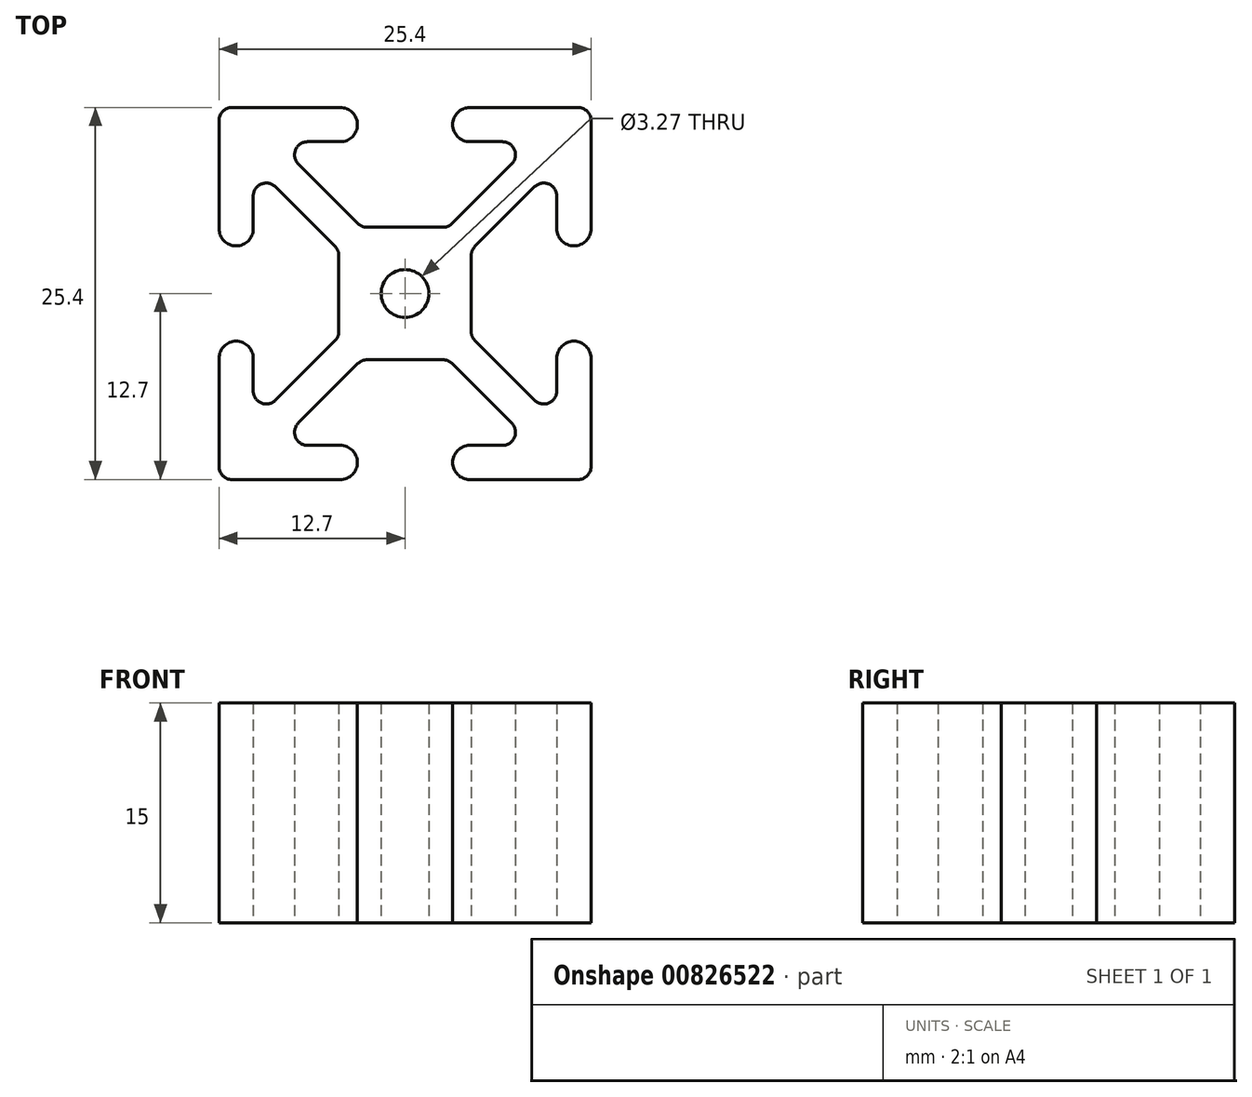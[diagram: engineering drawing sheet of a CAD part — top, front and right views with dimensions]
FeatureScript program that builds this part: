
annotation { "Feature Type Name" : "Feature", "Feature Type Description" : "" }
export const myFeature = defineFeature(function(context is Context, id is Id, definition is map)
    precondition{}
    {
        {
            assignVariable(context, id + "F0", {"name" : "SPINE_length", "anyValue" : 15});
        }
        {
            var Q0;
            Q0=qCreatedBy(makeId("Top.planeOp"),FACE);
            var sketch = newSketch(context, id + "F1", { "sketchPlane" : qUnion([Q0])});
            skCircle(sketch, "E0", {"center": v(0, 0) * mm, "radius": 1.63 * mm});
            skLineSegment(sketch, "E1.bottom", {"start": v(2.6, -4.52) * mm, "end": v(-2.6, -4.52) * mm});
            skLineSegment(sketch, "E1.top", {"start": v(2.6, 4.52) * mm, "end": v(-2.6, 4.52) * mm});
            skLineSegment(sketch, "E1.left", {"start": v(4.52, -2.6) * mm, "end": v(4.52, 2.6) * mm});
            skLineSegment(sketch, "E1.right", {"start": v(-4.52, -2.6) * mm, "end": v(-4.52, 2.6) * mm});
            skLineSegment(sketch, "E2", {"start": v(-3.22, -4.78) * mm, "end": v(-7.28, -8.85) * mm});
            skLineSegment(sketch, "E3", {"start": v(-4.78, -3.22) * mm, "end": v(-8.85, -7.28) * mm});
            skLineSegment(sketch, "E4", {"start": v(-4.52, -4.52) * mm, "end": v(4.52, 4.52) * mm, "construction": true});
            skLineSegment(sketch, "E5", {"start": v(-4.52, 4.52) * mm, "end": v(4.52, -4.52) * mm, "construction": true});
            skLineSegment(sketch, "E6", {"start": v(-3.22, 4.78) * mm, "end": v(-7.28, 8.85) * mm});
            skLineSegment(sketch, "E7", {"start": v(-4.78, 3.22) * mm, "end": v(-8.85, 7.28) * mm});
            skLineSegment(sketch, "E8", {"start": v(3.22, 4.78) * mm, "end": v(7.28, 8.85) * mm});
            skLineSegment(sketch, "E9", {"start": v(4.78, 3.22) * mm, "end": v(8.85, 7.28) * mm});
            skLineSegment(sketch, "E10", {"start": v(4.78, -3.22) * mm, "end": v(8.85, -7.28) * mm});
            skLineSegment(sketch, "E11", {"start": v(3.22, -4.78) * mm, "end": v(7.28, -8.85) * mm});
            skLineSegment(sketch, "E12", {"start": v(-6.65, -10.36) * mm, "end": v(-4.42, -10.36) * mm});
            skLineSegment(sketch, "E13", {"start": v(-10.36, -6.65) * mm, "end": v(-10.36, -4.42) * mm});
            skLineSegment(sketch, "E14", {"start": v(-10.36, 6.65) * mm, "end": v(-10.36, 4.42) * mm});
            skLineSegment(sketch, "E15", {"start": v(-6.65, 10.36) * mm, "end": v(-4.42, 10.36) * mm});
            skLineSegment(sketch, "E16", {"start": v(6.65, 10.36) * mm, "end": v(4.42, 10.36) * mm});
            skLineSegment(sketch, "E17", {"start": v(10.36, 6.65) * mm, "end": v(10.36, 4.42) * mm});
            skLineSegment(sketch, "E18", {"start": v(10.36, -6.65) * mm, "end": v(10.36, -4.42) * mm});
            skLineSegment(sketch, "E19", {"start": v(6.65, -10.36) * mm, "end": v(4.42, -10.36) * mm});
            skLineSegment(sketch, "E20", {"start": v(-4.42, 12.7) * mm, "end": v(-11.81, 12.7) * mm});
            skLineSegment(sketch, "E21", {"start": v(-12.7, 11.81) * mm, "end": v(-12.7, 4.42) * mm});
            skLineSegment(sketch, "E22", {"start": v(-12.7, -11.81) * mm, "end": v(-12.7, -4.42) * mm});
            skLineSegment(sketch, "E23", {"start": v(-11.81, -12.7) * mm, "end": v(-4.42, -12.7) * mm});
            skLineSegment(sketch, "E24", {"start": v(11.81, -12.7) * mm, "end": v(4.42, -12.7) * mm});
            skLineSegment(sketch, "E25", {"start": v(12.7, -11.81) * mm, "end": v(12.7, -4.42) * mm});
            skLineSegment(sketch, "E26", {"start": v(12.7, 11.81) * mm, "end": v(12.7, 4.42) * mm});
            skLineSegment(sketch, "E27", {"start": v(11.81, 12.7) * mm, "end": v(4.42, 12.7) * mm});
            skLineSegment(sketch, "E28", {"start": v(-11.48, 3.25) * mm, "end": v(-11.48, 3.25) * mm});
            skLineSegment(sketch, "E29", {"start": v(-11.59, -3.25) * mm, "end": v(-11.59, -3.25) * mm});
            skLineSegment(sketch, "E30", {"start": v(-3.25, -11.53) * mm, "end": v(-3.25, -11.53) * mm});
            skLineSegment(sketch, "E31", {"start": v(3.25, -11.53) * mm, "end": v(3.25, -11.53) * mm});
            skLineSegment(sketch, "E32", {"start": v(11.53, -3.25) * mm, "end": v(11.53, -3.25) * mm});
            skLineSegment(sketch, "E33", {"start": v(11.53, 3.25) * mm, "end": v(11.53, 3.25) * mm});
            skLineSegment(sketch, "E34", {"start": v(3.25, 11.53) * mm, "end": v(3.25, 11.53) * mm});
            skLineSegment(sketch, "E35", {"start": v(-3.25, 11.53) * mm, "end": v(-3.25, 11.53) * mm});
            skPoint(sketch, "E36.visualSharp", {"position": v(-8.8, 10.36) * mm});
            skArc(sketch, "E36.filletArc", {"start": v(-6.65, 10.36) * mm, "mid": v(-7.48, 9.81) * mm, "end": v(-7.28, 8.85) * mm});
            skPoint(sketch, "E37.visualSharp", {"position": v(8.8, 10.36) * mm});
            skArc(sketch, "E37.filletArc", {"start": v(7.28, 8.85) * mm, "mid": v(7.48, 9.81) * mm, "end": v(6.65, 10.36) * mm});
            skPoint(sketch, "E38.visualSharp", {"position": v(10.36, 8.8) * mm});
            skArc(sketch, "E38.filletArc", {"start": v(10.36, 6.65) * mm, "mid": v(9.81, 7.48) * mm, "end": v(8.85, 7.28) * mm});
            skPoint(sketch, "E39.visualSharp", {"position": v(10.36, -8.8) * mm});
            skArc(sketch, "E39.filletArc", {"start": v(8.85, -7.28) * mm, "mid": v(9.81, -7.48) * mm, "end": v(10.36, -6.65) * mm});
            skPoint(sketch, "E40.visualSharp", {"position": v(8.8, -10.36) * mm});
            skArc(sketch, "E40.filletArc", {"start": v(6.65, -10.36) * mm, "mid": v(7.48, -9.81) * mm, "end": v(7.28, -8.85) * mm});
            skPoint(sketch, "E41.visualSharp", {"position": v(-10.36, -8.8) * mm});
            skArc(sketch, "E41.filletArc", {"start": v(-10.36, -6.65) * mm, "mid": v(-9.81, -7.48) * mm, "end": v(-8.85, -7.28) * mm});
            skPoint(sketch, "E42.visualSharp", {"position": v(-8.8, -10.36) * mm});
            skArc(sketch, "E42.filletArc", {"start": v(-7.28, -8.85) * mm, "mid": v(-7.48, -9.81) * mm, "end": v(-6.65, -10.36) * mm});
            skPoint(sketch, "E43.visualSharp", {"position": v(-10.36, 8.8) * mm});
            skArc(sketch, "E43.filletArc", {"start": v(-8.85, 7.28) * mm, "mid": v(-9.81, 7.48) * mm, "end": v(-10.36, 6.65) * mm});
            skPoint(sketch, "E44.visualSharp", {"position": v(-12.7, 12.7) * mm});
            skArc(sketch, "E44.filletArc", {"start": v(-11.81, 12.7) * mm, "mid": v(-12.44, 12.44) * mm, "end": v(-12.7, 11.81) * mm});
            skPoint(sketch, "E45.visualSharp", {"position": v(12.7, 12.7) * mm});
            skArc(sketch, "E45.filletArc", {"start": v(12.7, 11.81) * mm, "mid": v(12.44, 12.44) * mm, "end": v(11.81, 12.7) * mm});
            skPoint(sketch, "E46.visualSharp", {"position": v(12.7, -12.7) * mm});
            skArc(sketch, "E46.filletArc", {"start": v(11.81, -12.7) * mm, "mid": v(12.44, -12.44) * mm, "end": v(12.7, -11.81) * mm});
            skPoint(sketch, "E47.visualSharp", {"position": v(-12.7, -12.7) * mm});
            skArc(sketch, "E47.filletArc", {"start": v(-12.7, -11.81) * mm, "mid": v(-12.44, -12.44) * mm, "end": v(-11.81, -12.7) * mm});
            skPoint(sketch, "E48.newPointB", {"position": v(-6.36, 4.52) * mm});
            skArc(sketch, "E48.filletArc", {"start": v(-3.22, 4.78) * mm, "mid": v(-2.93, 4.59) * mm, "end": v(-2.6, 4.52) * mm});
            skPoint(sketch, "E49.newPointB", {"position": v(2.6, 4.52) * mm});
            skArc(sketch, "E49.filletArc", {"start": v(2.6, 4.52) * mm, "mid": v(2.93, 4.59) * mm, "end": v(3.22, 4.78) * mm});
            skArc(sketch, "E50.filletArc", {"start": v(4.78, 3.22) * mm, "mid": v(4.59, 2.93) * mm, "end": v(4.52, 2.6) * mm});
            skArc(sketch, "E51.filletArc", {"start": v(-4.78, -3.22) * mm, "mid": v(-4.59, -2.93) * mm, "end": v(-4.52, -2.6) * mm});
            skPoint(sketch, "E52.newPointA", {"position": v(-2.6, -4.52) * mm});
            skArc(sketch, "E52.filletArc", {"start": v(-2.6, -4.52) * mm, "mid": v(-2.93, -4.59) * mm, "end": v(-3.22, -4.78) * mm});
            skArc(sketch, "E53.filletArc", {"start": v(4.52, -2.6) * mm, "mid": v(4.59, -2.93) * mm, "end": v(4.78, -3.22) * mm});
            skPoint(sketch, "E54.newPointA", {"position": v(6.36, -4.52) * mm});
            skArc(sketch, "E54.filletArc", {"start": v(3.22, -4.78) * mm, "mid": v(2.93, -4.59) * mm, "end": v(2.6, -4.52) * mm});
            skArc(sketch, "E55.filletArc", {"start": v(-4.52, 2.6) * mm, "mid": v(-4.59, 2.93) * mm, "end": v(-4.78, 3.22) * mm});
            skPoint(sketch, "E56.visualSharp", {"position": v(-12.7, 3.2) * mm});
            skArc(sketch, "E56.filletArc", {"start": v(-12.7, 4.42) * mm, "mid": v(-12.34, 3.58) * mm, "end": v(-11.48, 3.25) * mm});
            skPoint(sketch, "E57.visualSharp", {"position": v(-10.36, 3.3) * mm});
            skArc(sketch, "E57.filletArc", {"start": v(-11.48, 3.25) * mm, "mid": v(-10.69, 3.61) * mm, "end": v(-10.36, 4.42) * mm});
            skPoint(sketch, "E58.visualSharp", {"position": v(-3.25, 12.7) * mm});
            skArc(sketch, "E58.filletArc", {"start": v(-3.25, 11.53) * mm, "mid": v(-3.6, 12.36) * mm, "end": v(-4.42, 12.7) * mm});
            skPoint(sketch, "E59.visualSharp", {"position": v(-3.25, 10.36) * mm});
            skArc(sketch, "E59.filletArc", {"start": v(-4.42, 10.36) * mm, "mid": v(-3.6, 10.7) * mm, "end": v(-3.25, 11.53) * mm});
            skPoint(sketch, "E60.visualSharp", {"position": v(3.25, 10.36) * mm});
            skArc(sketch, "E60.filletArc", {"start": v(3.25, 11.53) * mm, "mid": v(3.6, 10.7) * mm, "end": v(4.42, 10.36) * mm});
            skPoint(sketch, "E61.visualSharp", {"position": v(3.25, 12.7) * mm});
            skArc(sketch, "E61.filletArc", {"start": v(4.42, 12.7) * mm, "mid": v(3.6, 12.36) * mm, "end": v(3.25, 11.53) * mm});
            skPoint(sketch, "E62.visualSharp", {"position": v(10.36, 3.25) * mm});
            skArc(sketch, "E62.filletArc", {"start": v(10.36, 4.42) * mm, "mid": v(10.7, 3.6) * mm, "end": v(11.53, 3.25) * mm});
            skPoint(sketch, "E63.visualSharp", {"position": v(12.7, 3.25) * mm});
            skArc(sketch, "E63.filletArc", {"start": v(11.53, 3.25) * mm, "mid": v(12.36, 3.6) * mm, "end": v(12.7, 4.42) * mm});
            skPoint(sketch, "E64.visualSharp", {"position": v(12.7, -3.25) * mm});
            skArc(sketch, "E64.filletArc", {"start": v(12.7, -4.42) * mm, "mid": v(12.36, -3.6) * mm, "end": v(11.53, -3.25) * mm});
            skPoint(sketch, "E65.visualSharp", {"position": v(10.36, -3.25) * mm});
            skArc(sketch, "E65.filletArc", {"start": v(11.53, -3.25) * mm, "mid": v(10.7, -3.6) * mm, "end": v(10.36, -4.42) * mm});
            skPoint(sketch, "E66.visualSharp", {"position": v(3.25, -10.36) * mm});
            skArc(sketch, "E66.filletArc", {"start": v(4.42, -10.36) * mm, "mid": v(3.6, -10.7) * mm, "end": v(3.25, -11.53) * mm});
            skPoint(sketch, "E67.visualSharp", {"position": v(3.25, -12.7) * mm});
            skArc(sketch, "E67.filletArc", {"start": v(3.25, -11.53) * mm, "mid": v(3.6, -12.36) * mm, "end": v(4.42, -12.7) * mm});
            skPoint(sketch, "E68.visualSharp", {"position": v(-3.25, -12.7) * mm});
            skArc(sketch, "E68.filletArc", {"start": v(-4.42, -12.7) * mm, "mid": v(-3.6, -12.36) * mm, "end": v(-3.25, -11.53) * mm});
            skPoint(sketch, "E69.visualSharp", {"position": v(-3.25, -10.36) * mm});
            skArc(sketch, "E69.filletArc", {"start": v(-3.25, -11.53) * mm, "mid": v(-3.6, -10.7) * mm, "end": v(-4.42, -10.36) * mm});
            skPoint(sketch, "E70.visualSharp", {"position": v(-10.36, -3.2) * mm});
            skArc(sketch, "E70.filletArc", {"start": v(-10.36, -4.42) * mm, "mid": v(-10.73, -3.58) * mm, "end": v(-11.59, -3.25) * mm});
            skPoint(sketch, "E71.visualSharp", {"position": v(-12.7, -3.3) * mm});
            skArc(sketch, "E71.filletArc", {"start": v(-11.59, -3.25) * mm, "mid": v(-12.38, -3.61) * mm, "end": v(-12.7, -4.42) * mm});
            skSolve(sketch);
        }
        {
            var Q0;
            Q0 = qSketchRegion(id + "F1", true);
            extrude(context, id + "F2", {"entities" : qUnion([Q0]), "depth" : (getVariable(context, 'SPINE_length')) * mm, "offsetDistance" : 25.4 * mm});
        }
    });
